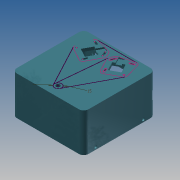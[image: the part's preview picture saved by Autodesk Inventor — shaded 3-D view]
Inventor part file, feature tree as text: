
AUTODESK INVENTOR PART (.ipt)
format: ipt  version: 2013 (Build 170138000, 138)  size: 740,352 bytes
history: native  units: mm
features: extrude x27, sketch x27, chamfer x4, reference x4, fillet x3, plane x3, mirror x2, projected_geometry x2, pattern_linear x1, other x1
ambient origin geometry x8: Origin, YZ Plane, XZ Plane, XY Plane, X Axis, Y Axis, Z Axis, Center Point
bodies: Solid1 (feature_tree)
feature tree (74):
  extrude  "Extrusion1"  Depth=42.0mm
  fillet  "Fillet1"  Radius=31.0mm
  extrude  "Extrusion2"  Depth=5.5mm
  extrude  "Extrusion3"  Depth=3.5mm
  mirror  "Mirror1"
  sketch  "Sketch4"  dims[d8=5.5mm d9=5.5mm]
  extrude  "Extrusion4"  Depth=5.5mm
  extrude  "Extrusion22"  Depth=5.5mm
  extrude  "Extrusion23"  Depth=5.0mm TaperAngle=0.0deg
  fillet  "Fillet2"  Radius=15.0mm
  extrude  "Extrusion24"  Depth=8.5mm
  extrude  "Extrusion25"  Depth=5.0mm
  extrude  "Extrusion26"  Depth=10.0mm TaperAngle=0.0deg
  extrude  "Extrusion28"  Depth=5.0mm
  extrude  "Extrusion31"  Depth=12.5mm
  chamfer  "Chamfer2"  Distance=30.0mm
  sketch  "Sketch32"  dims[d121=1.0mm d122=2.0mm d123=45.0deg d124=3.0mm]
  plane  "Work Plane4"
  extrude  "Extrusion32"  Depth=8.0mm TaperAngle=0.0deg
  chamfer  "Chamfer3"  Distance=1.0mm
  extrude  "Extrusion33"  Depth=3.0mm
  extrude  "Extrusion34"  Depth=5.0mm
  sketch  "Sketch35"  dims[d141=0.5mm d142=8.6mm d143=0.0mm]
  extrude  "Extrusion35"  Depth=5.6mm TaperAngle=45.0deg
  extrude  "Extrusion36"  Depth=8.6mm TaperAngle=0.0deg
  extrude  "Extrusion37"  Depth=8.6mm TaperAngle=0.0deg
  extrude  "Extrusion38"  Depth=8.6mm TaperAngle=0.0deg
  extrude  "Extrusion39"  Depth=1.0mm
  mirror  "Mirror3"
  extrude  "Extrusion40"  Depth=8.6mm TaperAngle=0.0deg
  extrude  "Extrusion41"  Depth=42.96mm
  extrude  "Extrusion42"  Depth=8.0mm
  chamfer  "Chamfer4"  Distance=10.0mm
  fillet  "Fillet3"  Radius=10.0mm
  extrude  "Extrusion43"  Depth=36.0mm
  extrude  "Extrusion44"  Depth=3.0mm TaperAngle=0.0deg
  extrude  "Extrusion45"  Depth=15.0mm
  extrude  "Extrusion46"  Depth=10.5mm
  pattern_linear  "Rectangular Pattern1"  Spacing1=4.0mm  [1 undecoded]
  other  "Work Axis2"
  extrude  "Extrusion27"  Depth=8.0mm
  chamfer  "Chamfer1"  Distance=4.0mm
  sketch  "Sketch1"  dims[d0=198.0mm d2=42.0mm d3=31.0mm]
  sketch  "Sketch2"  dims[d4=5.5mm d5=5.5mm]
  sketch  "Sketch3"  dims[d6=5.0mm d7=3.5mm]
  projected_geometry  "Projected Loop1"
  sketch  "Sketch22"  dims[d10=6.0mm d11=0.0mm d12=5.5mm]
  sketch  "Sketch23"  dims[d13=5.0mm d14=0.0mm d15=5.0mm d16=0.0mm d17=15.0mm]
  sketch  "Sketch24"  dims[d19=5.0mm d20=0.0mm d100=8.5mm]
  sketch  "Sketch25"  dims[d102=10.0mm d103=0.0mm d104=5.0mm]
  sketch  "Sketch26"  dims[d105=150.0mm d106=10.0mm d107=0.0mm]
  plane  "Work Plane2"
  plane  "Work Plane3"
  sketch  "Sketch27"  dims[d108=10.0mm d109=5.0mm]
  sketch  "Sketch28"  dims[d110=75.0mm d111=0.0mm d112=12.5mm d114=30.0mm d115=0.0mm]
  sketch  "Sketch31"  dims[d116=13.0mm d117=8.0mm d118=0.0mm d119=1.0mm d120=0.0mm]
  reference  "Reference4"
  projected_geometry  "Projected Loop4"
  reference  "Reference5"
  sketch  "Sketch33"  dims[d126=3.0mm d127=0.0mm d135=5.0mm]
  reference  "Reference6"
  sketch  "Sketch34"  dims[d136=5.6mm d137=0.0mm d138=5.6mm d139=2.0mm d140=45.0deg]
  reference  "Reference7"
  sketch  "Sketch36"  dims[d144=8.6mm d145=2.0mm d146=45.0deg d147=8.6mm d148=0.0mm]
  sketch  "Sketch37"  dims[d149=3.0mm d150=8.6mm d151=0.0mm]
  sketch  "Sketch38"  dims[d152=1.0mm d153=1.0mm]
  sketch  "Sketch39"  dims[d154=8.6mm d155=0.0mm d156=8.6mm d157=0.0mm]
  sketch  "Sketch40"  dims[d158=88.88mm d160=42.96mm]
  sketch  "Sketch41"  dims[d161=3.0mm d162=8.0mm]
  sketch  "Sketch42"  dims[d163=40.0mm d164=10.0mm d165=0.0mm d166=10.0mm]
  sketch  "Sketch43"  dims[d169=5.0mm d170=36.0mm]
  sketch  "Sketch44"  dims[d171=3.0mm d172=0.0mm d173=3.0mm d174=0.0mm]
  sketch  "Sketch45"  dims[d175=12.0mm d177=15.0mm]
  sketch  "Sketch46"  dims[d178=3.0mm d179=10.5mm d180=4.0mm d181=0.0mm d182=8.0mm d184=4.0mm d185=0.0mm d187=3.1mm d188=0.0mm d189=2.0mm d190=2.0mm d191=45.0deg d192=2.0mm d193=3.5mm d195=100.0mm d196=5.0mm d197=3.1mm d198=0.0mm d199=6.0mm d201=3.0mm d202=0.0mm d203=3.0mm d204=0.0mm d205=10.0mm d206=3.0mm d207=0.0mm d208=50.0mm d210=25.0mm d211=30.0mm d213=20.0mm]
note: 1 required parameter value undecoded (feature->parameter linkage not recoverable at this tier; creation-order binding heuristic only, values carry confidence <= 0.55)
